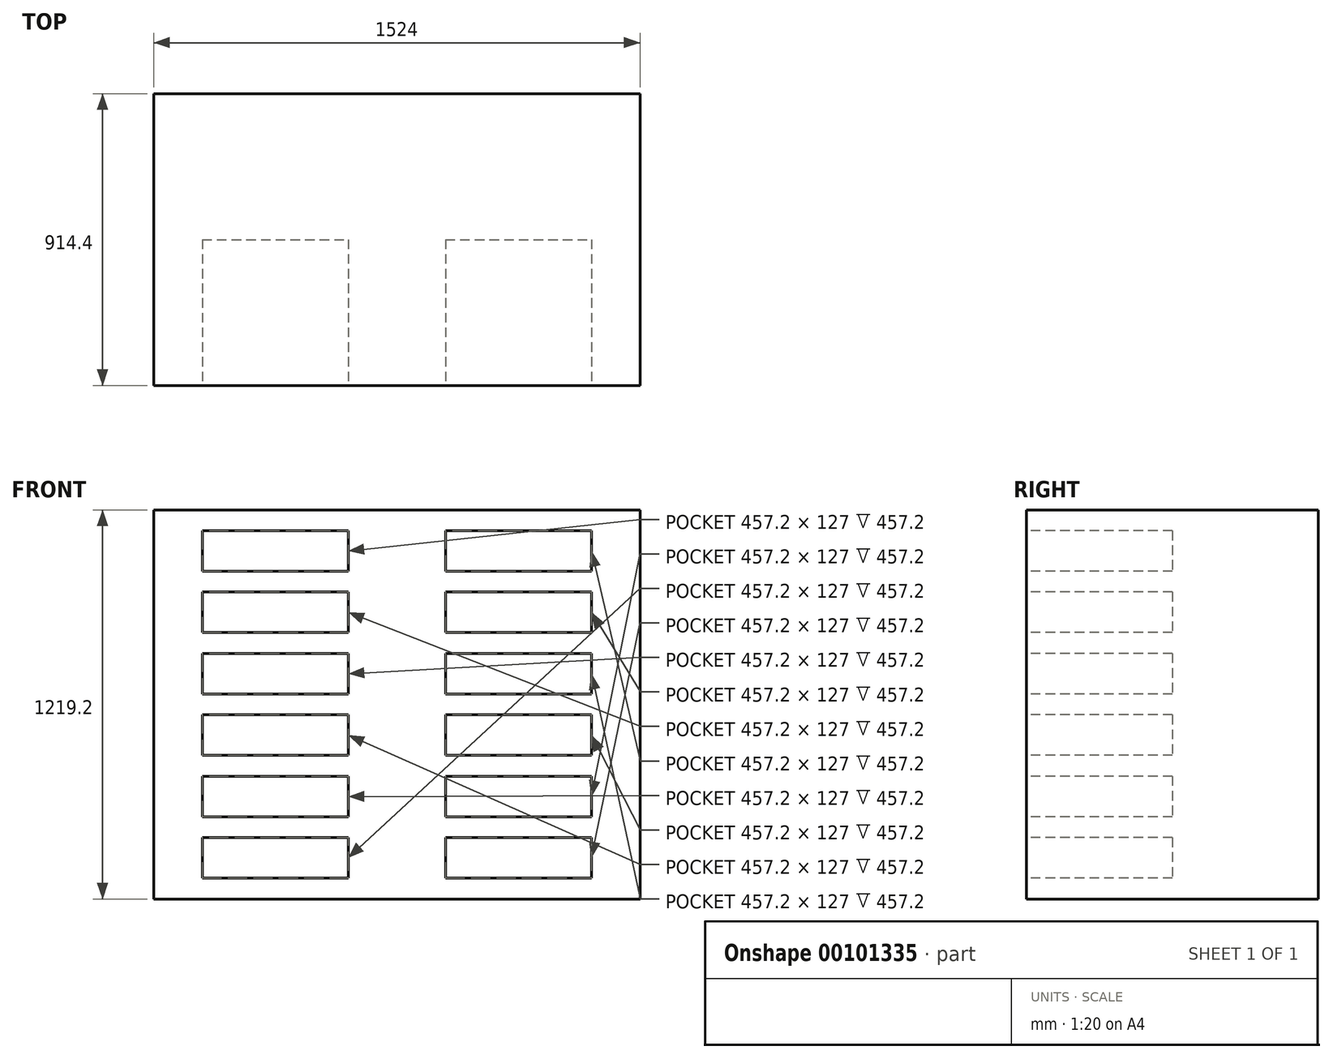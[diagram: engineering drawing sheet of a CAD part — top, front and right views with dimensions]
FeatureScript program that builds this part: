
annotation { "Feature Type Name" : "Feature", "Feature Type Description" : "" }
export const myFeature = defineFeature(function(context is Context, id is Id, definition is map)
    precondition{}
    {
        {
            var Q0;
            Q0=qCreatedBy(makeId("Front.planeOp"),FACE);
            var sketch = newSketch(context, id + "F0", { "sketchPlane" : qUnion([Q0])});
            skLineSegment(sketch, "E0.bottom", {"start": v(-762, 609.6) * mm, "end": v(762, 609.6) * mm});
            skLineSegment(sketch, "E0.top", {"start": v(-762, -609.6) * mm, "end": v(762, -609.6) * mm});
            skLineSegment(sketch, "E0.left", {"start": v(-762, 609.6) * mm, "end": v(-762, -609.6) * mm});
            skLineSegment(sketch, "E0.right", {"start": v(762, 609.6) * mm, "end": v(762, -609.6) * mm});
            skSolve(sketch);
        }
        {
            var Q0;
            Q0 = qSketchRegion(id + "F0", true);
            extrude(context, id + "F1", {"entities" : qUnion([Q0]), "depth" : 914.4 * mm});
        }
        {
            var Q0;
            Q0=makeQuery(id+"F1.opExtrude","CAP_FACE",FACE,{"disambiguationData":[OSD([sQuery(id+"F0.wireOp",EDGE,"E0.bottom"),sQuery(id+"F0.wireOp",EDGE,"E0.top"),sQuery(id+"F0.wireOp",EDGE,"E0.left"),sQuery(id+"F0.wireOp",EDGE,"E0.right")])],"isStart":false});
            var sketch = newSketch(context, id + "F2", { "sketchPlane" : qUnion([Q0])});
            skLineSegment(sketch, "E1.bottom", {"start": v(-609.6, 544.32) * mm, "end": v(-152.4, 544.32) * mm});
            skLineSegment(sketch, "E1.top", {"start": v(-609.6, 417.32) * mm, "end": v(-152.4, 417.32) * mm});
            skLineSegment(sketch, "E1.left", {"start": v(-609.6, 544.32) * mm, "end": v(-609.6, 417.32) * mm});
            skLineSegment(sketch, "E1.right", {"start": v(-152.4, 544.32) * mm, "end": v(-152.4, 417.32) * mm});
            skLineSegment(sketch, "E2.bottom", {"start": v(152.4, 544.32) * mm, "end": v(609.6, 544.32) * mm});
            skLineSegment(sketch, "E2.top", {"start": v(152.4, 417.32) * mm, "end": v(609.6, 417.32) * mm});
            skLineSegment(sketch, "E2.left", {"start": v(152.4, 544.32) * mm, "end": v(152.4, 417.32) * mm});
            skLineSegment(sketch, "E2.right", {"start": v(609.6, 544.32) * mm, "end": v(609.6, 417.32) * mm});
            skLineSegment(sketch, "E3.0.1.0", {"start": v(-609.6, 352) * mm, "end": v(-152.4, 352) * mm});
            skLineSegment(sketch, "E3.0.1.1", {"start": v(-152.4, 352) * mm, "end": v(-152.4, 225) * mm});
            skLineSegment(sketch, "E3.0.1.2", {"start": v(-609.6, 225) * mm, "end": v(-152.4, 225) * mm});
            skLineSegment(sketch, "E3.0.1.3", {"start": v(-609.6, 352) * mm, "end": v(-609.6, 225) * mm});
            skLineSegment(sketch, "E3.0.1.4", {"start": v(152.4, 352) * mm, "end": v(609.6, 352) * mm});
            skLineSegment(sketch, "E3.0.1.5", {"start": v(152.4, 352) * mm, "end": v(152.4, 225) * mm});
            skLineSegment(sketch, "E3.0.1.6", {"start": v(609.6, 352) * mm, "end": v(609.6, 225) * mm});
            skLineSegment(sketch, "E3.0.1.7", {"start": v(152.4, 225) * mm, "end": v(609.6, 225) * mm});
            skLineSegment(sketch, "E3.0.2.0", {"start": v(-609.6, 159.7) * mm, "end": v(-152.4, 159.7) * mm});
            skLineSegment(sketch, "E3.0.2.1", {"start": v(-152.4, 159.7) * mm, "end": v(-152.4, 32.7) * mm});
            skLineSegment(sketch, "E3.0.2.2", {"start": v(-609.6, 32.7) * mm, "end": v(-152.4, 32.7) * mm});
            skLineSegment(sketch, "E3.0.2.3", {"start": v(-609.6, 159.7) * mm, "end": v(-609.6, 32.7) * mm});
            skLineSegment(sketch, "E3.0.2.4", {"start": v(152.4, 159.7) * mm, "end": v(609.6, 159.7) * mm});
            skLineSegment(sketch, "E3.0.2.5", {"start": v(152.4, 159.7) * mm, "end": v(152.4, 32.7) * mm});
            skLineSegment(sketch, "E3.0.2.6", {"start": v(609.6, 159.7) * mm, "end": v(609.6, 32.7) * mm});
            skLineSegment(sketch, "E3.0.2.7", {"start": v(152.4, 32.7) * mm, "end": v(609.6, 32.7) * mm});
            skLineSegment(sketch, "E3.0.3.0", {"start": v(-609.6, -32.62) * mm, "end": v(-152.4, -32.62) * mm});
            skLineSegment(sketch, "E3.0.3.1", {"start": v(-152.4, -32.62) * mm, "end": v(-152.4, -159.62) * mm});
            skLineSegment(sketch, "E3.0.3.2", {"start": v(-609.6, -159.62) * mm, "end": v(-152.4, -159.62) * mm});
            skLineSegment(sketch, "E3.0.3.3", {"start": v(-609.6, -32.62) * mm, "end": v(-609.6, -159.62) * mm});
            skLineSegment(sketch, "E3.0.3.4", {"start": v(152.4, -32.62) * mm, "end": v(609.6, -32.62) * mm});
            skLineSegment(sketch, "E3.0.3.5", {"start": v(152.4, -32.62) * mm, "end": v(152.4, -159.62) * mm});
            skLineSegment(sketch, "E3.0.3.6", {"start": v(609.6, -32.62) * mm, "end": v(609.6, -159.62) * mm});
            skLineSegment(sketch, "E3.0.3.7", {"start": v(152.4, -159.62) * mm, "end": v(609.6, -159.62) * mm});
            skLineSegment(sketch, "E3.0.4.0", {"start": v(-609.6, -224.94) * mm, "end": v(-152.4, -224.94) * mm});
            skLineSegment(sketch, "E3.0.4.1", {"start": v(-152.4, -224.94) * mm, "end": v(-152.4, -351.94) * mm});
            skLineSegment(sketch, "E3.0.4.2", {"start": v(-609.6, -351.94) * mm, "end": v(-152.4, -351.94) * mm});
            skLineSegment(sketch, "E3.0.4.3", {"start": v(-609.6, -224.94) * mm, "end": v(-609.6, -351.94) * mm});
            skLineSegment(sketch, "E3.0.4.4", {"start": v(152.4, -224.94) * mm, "end": v(609.6, -224.94) * mm});
            skLineSegment(sketch, "E3.0.4.5", {"start": v(152.4, -224.94) * mm, "end": v(152.4, -351.94) * mm});
            skLineSegment(sketch, "E3.0.4.6", {"start": v(609.6, -224.94) * mm, "end": v(609.6, -351.94) * mm});
            skLineSegment(sketch, "E3.0.4.7", {"start": v(152.4, -351.94) * mm, "end": v(609.6, -351.94) * mm});
            skLineSegment(sketch, "E3.0.5.0", {"start": v(-609.6, -417.25) * mm, "end": v(-152.4, -417.25) * mm});
            skLineSegment(sketch, "E3.0.5.1", {"start": v(-152.4, -417.25) * mm, "end": v(-152.4, -544.25) * mm});
            skLineSegment(sketch, "E3.0.5.2", {"start": v(-609.6, -544.25) * mm, "end": v(-152.4, -544.25) * mm});
            skLineSegment(sketch, "E3.0.5.3", {"start": v(-609.6, -417.25) * mm, "end": v(-609.6, -544.25) * mm});
            skLineSegment(sketch, "E3.0.5.4", {"start": v(152.4, -417.25) * mm, "end": v(609.6, -417.25) * mm});
            skLineSegment(sketch, "E3.0.5.5", {"start": v(152.4, -417.25) * mm, "end": v(152.4, -544.25) * mm});
            skLineSegment(sketch, "E3.0.5.6", {"start": v(609.6, -417.25) * mm, "end": v(609.6, -544.25) * mm});
            skLineSegment(sketch, "E3.0.5.7", {"start": v(152.4, -544.25) * mm, "end": v(609.6, -544.25) * mm});
            skLineSegment(sketch, "E3.direction1", {"start": v(-609.6, 544.32) * mm, "end": v(-584.2, 544.32) * mm, "construction": true});
            skLineSegment(sketch, "E3.direction2", {"start": v(-609.6, 544.32) * mm, "end": v(-609.6, 352) * mm, "construction": true});
            skSolve(sketch);
        }
        {
            var Q0;
            Q0 = qSketchRegion(id + "F2", true);
            extrude(context, id + "F3", {"entities" : qUnion([Q0]), "operationType" : NewBodyOperationType.REMOVE, "oppositeDirection" : true, "depth" : 457.2 * mm});
        }
    });
